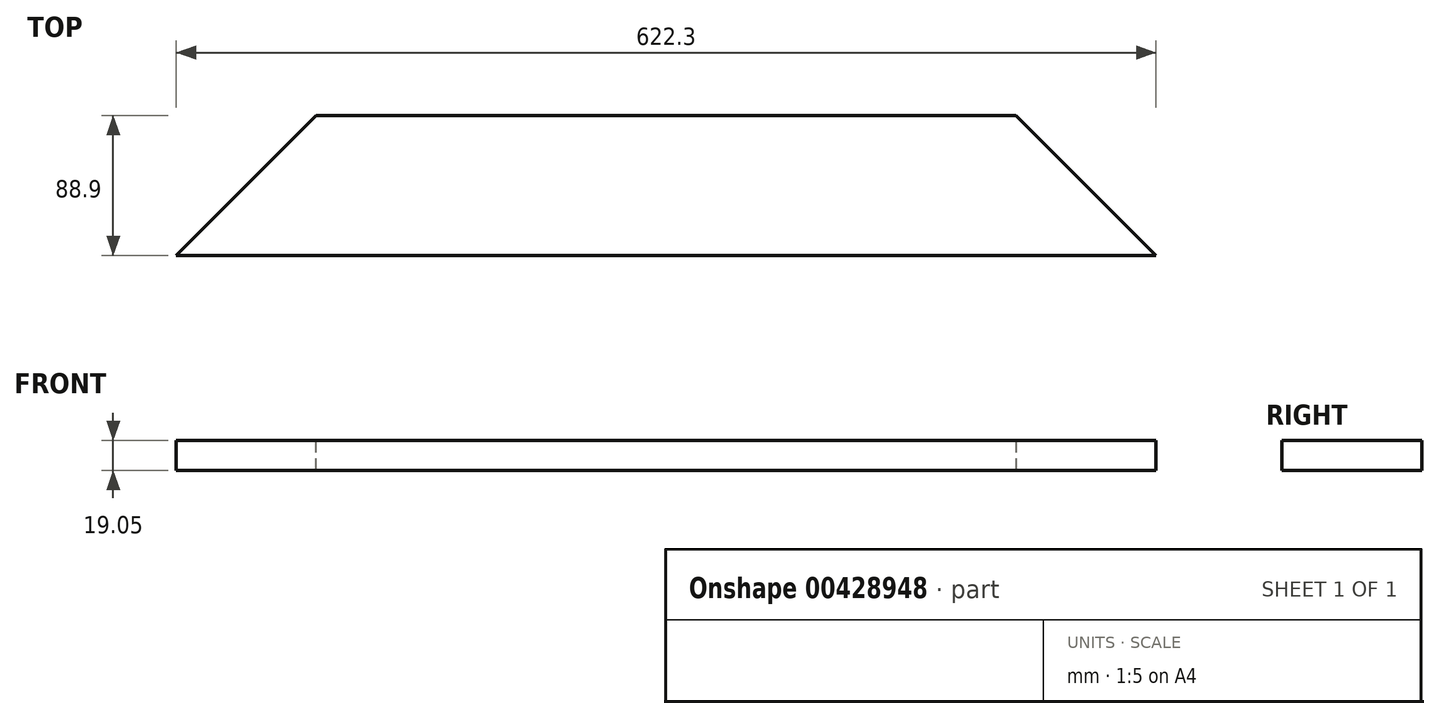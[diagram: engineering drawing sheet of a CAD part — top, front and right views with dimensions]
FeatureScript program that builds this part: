
annotation { "Feature Type Name" : "Feature", "Feature Type Description" : "" }
export const myFeature = defineFeature(function(context is Context, id is Id, definition is map)
    precondition{}
    {
        {
            var Q0;
            Q0=qCreatedBy(makeId("Top.planeOp"),FACE);
            var sketch = newSketch(context, id + "F0", { "sketchPlane" : qUnion([Q0])});
            skLineSegment(sketch, "E0.bottom", {"start": v(-532.8, 26.78) * mm, "end": v(89.5, 26.78) * mm});
            skLineSegment(sketch, "E0.top", {"start": v(-532.8, -62.12) * mm, "end": v(89.5, -62.12) * mm});
            skLineSegment(sketch, "E0.left", {"start": v(-532.8, 26.78) * mm, "end": v(-532.8, -62.12) * mm});
            skLineSegment(sketch, "E0.right", {"start": v(89.5, 26.78) * mm, "end": v(89.5, -62.12) * mm});
            skSolve(sketch);
        }
        {
            var Q0;
            Q0=makeQuery(id+"F0.imprint","IMPRINT",FACE,{"disambiguationData":[TD([[makeQuery(id+"F0.imprint","IMPRINT",EDGE,{"derivedFrom":sQuery(id+"F0.wireOp",EDGE,"E0.bottom")}),-1.0]])]});
            extrude(context, id + "F1", {"entities" : qUnion([Q0]), "depth" : 19.05 * mm});
        }
        {
            var Q0;
            Q0=makeQuery(id+"F1.opExtrude","SWEPT_EDGE",EDGE,{"disambiguationData":[OSD([sQuery(id+"F0.wireOp",EDGE,"E0.bottom"),sQuery(id+"F0.wireOp",EDGE,"E0.left")])]});
            chamfer(context, id + "F2", {"entities" : qUnion([Q0]), "width" : 88.9 * mm, "tangentPropagation" : true});
        }
        {
            var Q0;
            Q0=makeQuery(id+"F1.opExtrude","SWEPT_EDGE",EDGE,{"disambiguationData":[OSD([sQuery(id+"F0.wireOp",EDGE,"E0.bottom"),sQuery(id+"F0.wireOp",EDGE,"E0.right")])]});
            chamfer(context, id + "F3", {"entities" : qUnion([Q0]), "width" : 88.9 * mm, "tangentPropagation" : true});
        }
    });
